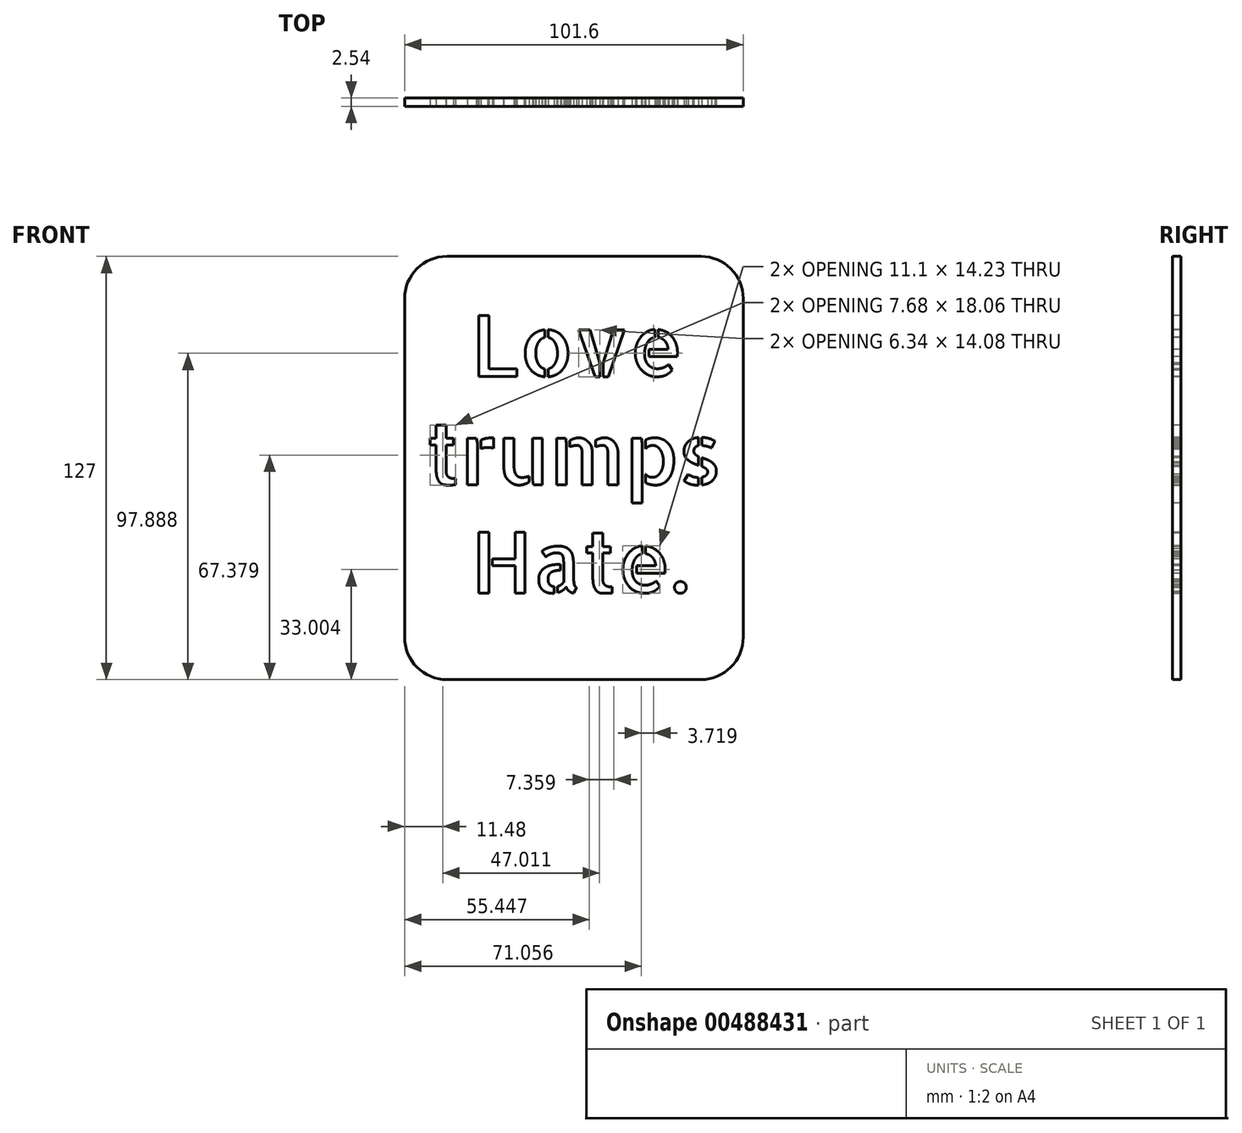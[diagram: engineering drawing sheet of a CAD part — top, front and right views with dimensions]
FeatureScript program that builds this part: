
annotation { "Feature Type Name" : "Feature", "Feature Type Description" : "" }
export const myFeature = defineFeature(function(context is Context, id is Id, definition is map)
    precondition{}
    {
        {
            var Q0;
            Q0=qCreatedBy(makeId("Front.planeOp"),FACE);
            var sketch = newSketch(context, id + "F0", { "sketchPlane" : qUnion([Q0])});
            skLineSegment(sketch, "E0.bottom", {"start": v(0, 0) * mm, "end": v(-101.6, 0) * mm});
            skLineSegment(sketch, "E0.top", {"start": v(0, 127) * mm, "end": v(-101.6, 127) * mm});
            skLineSegment(sketch, "E0.left", {"start": v(0, 0) * mm, "end": v(0, 127) * mm});
            skLineSegment(sketch, "E0.right", {"start": v(-101.6, 0) * mm, "end": v(-101.6, 127) * mm});
            skSolve(sketch);
        }
        {
            var Q0;
            Q0 = qSketchRegion(id + "F0", true);
            extrude(context, id + "F1", {"entities" : qUnion([Q0]), "depth" : 2.54 * mm});
        }
        {
            var Q0;
            Q0=makeQuery(id+"F1.opExtrude","CAP_FACE",FACE,{"disambiguationData":[OSD([sQuery(id+"F0.wireOp",EDGE,"E0.bottom"),sQuery(id+"F0.wireOp",EDGE,"E0.top"),sQuery(id+"F0.wireOp",EDGE,"E0.left"),sQuery(id+"F0.wireOp",EDGE,"E0.right")])],"isStart":false});
            var sketch = newSketch(context, id + "F2", { "sketchPlane" : qUnion([Q0])});
            skText(sketch, "E1", { "text": "  Love\ntrumps\n  Hate.", "fontName": "AllertaStencil-Regular.ttf"});
            const initialGuessF2  = {"E1": [-0.09525, 0.09095, 1, 0, 0.01827]};
            skSetInitialGuess(sketch, initialGuessF2);
            skSolve(sketch);
        }
        {
            var Q0;
            Q0 = qSketchRegion(id + "F2", true);
            extrude(context, id + "F3", {"entities" : qUnion([Q0]), "operationType" : NewBodyOperationType.REMOVE, "endBound" : BoundingType.THROUGH_ALL, "oppositeDirection" : true, "depth" : 25.4 * mm});
        }
        {
            var Q0;
            Q0=makeQuery(id+"F1.opExtrude","SWEPT_EDGE",EDGE,{"disambiguationData":[OSD([sQuery(id+"F0.wireOp",EDGE,"E0.top"),sQuery(id+"F0.wireOp",EDGE,"E0.right")])]});
            var Q1;
            Q1=makeQuery(id+"F1.opExtrude","SWEPT_EDGE",EDGE,{"disambiguationData":[OSD([sQuery(id+"F0.wireOp",EDGE,"E0.top"),sQuery(id+"F0.wireOp",EDGE,"E0.left")])]});
            var Q2;
            Q2=makeQuery(id+"F1.opExtrude","SWEPT_EDGE",EDGE,{"disambiguationData":[OSD([sQuery(id+"F0.wireOp",EDGE,"E0.bottom"),sQuery(id+"F0.wireOp",EDGE,"E0.right")])]});
            var Q3;
            Q3=makeQuery(id+"F1.opExtrude","SWEPT_EDGE",EDGE,{"disambiguationData":[OSD([sQuery(id+"F0.wireOp",EDGE,"E0.bottom"),sQuery(id+"F0.wireOp",EDGE,"E0.left")])]});
            fillet(context, id + "F4", {"entities" : qUnion([Q0, Q1, Q2, Q3]), "radius" : 12.7 * mm, "tangentPropagation" : true, "allowEdgeOverflow" : false});
        }
    });
